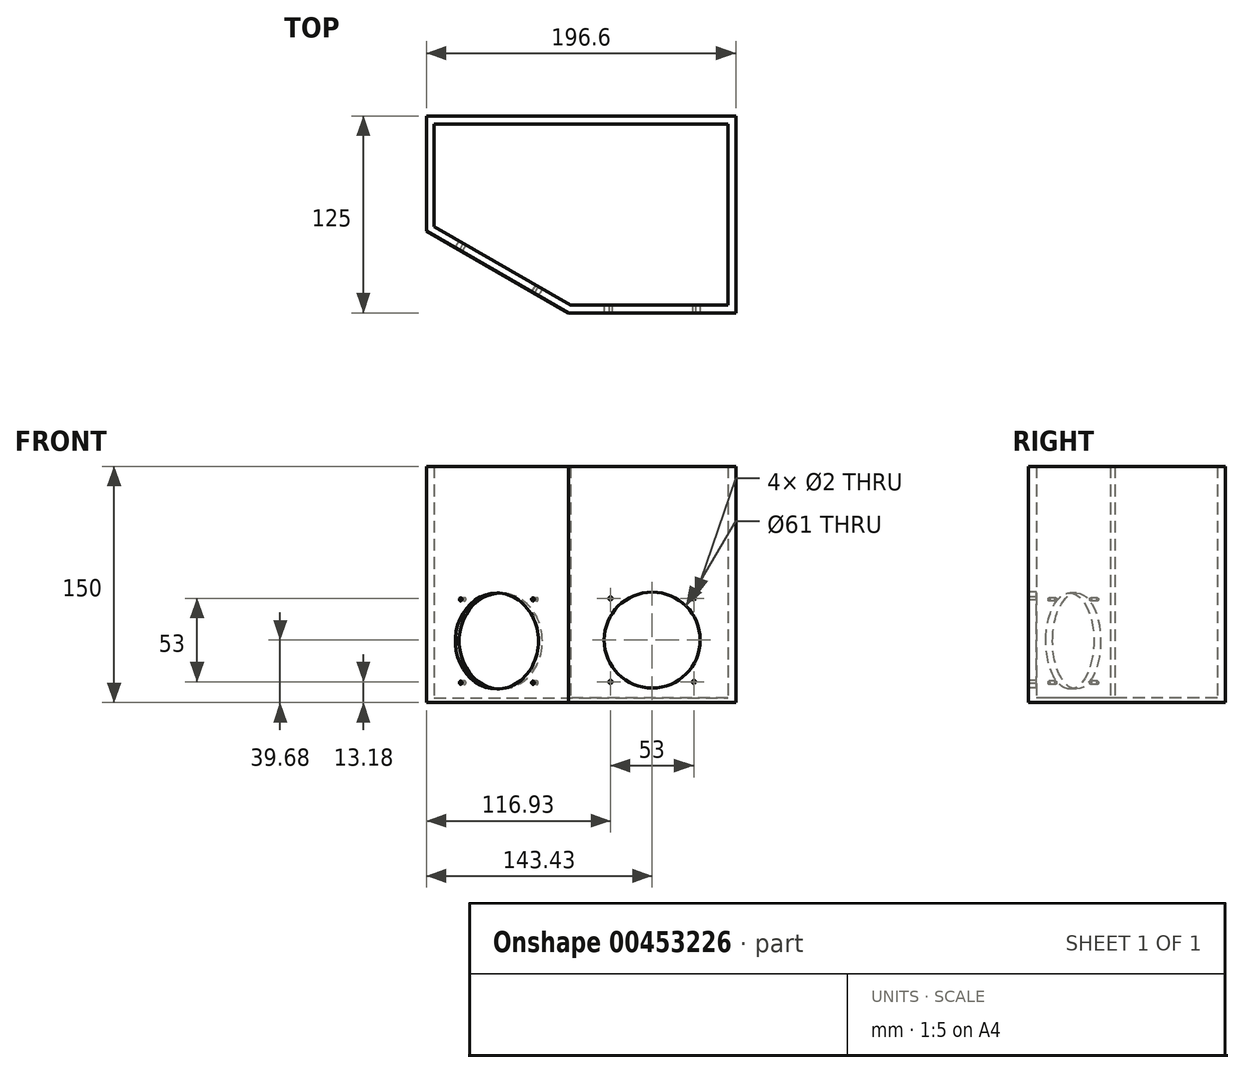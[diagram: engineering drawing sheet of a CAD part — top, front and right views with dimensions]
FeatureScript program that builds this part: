
annotation { "Feature Type Name" : "Feature", "Feature Type Description" : "" }
export const myFeature = defineFeature(function(context is Context, id is Id, definition is map)
    precondition{}
    {
        {
            var Q0;
            Q0=qCreatedBy(makeId("Top.planeOp"),FACE);
            var sketch = newSketch(context, id + "F0", { "sketchPlane" : qUnion([Q0])});
            skLineSegment(sketch, "E0", {"start": v(0, -81.78) * mm, "end": v(100, -81.78) * mm});
            skLineSegment(sketch, "E1", {"start": v(0, -81.78) * mm, "end": v(-86.6, -31.78) * mm});
            skLineSegment(sketch, "E2", {"start": v(100, -81.78) * mm, "end": v(100, 33.22) * mm});
            skLineSegment(sketch, "E3", {"start": v(100, 33.22) * mm, "end": v(-86.6, 33.22) * mm});
            skLineSegment(sketch, "E4", {"start": v(-86.6, -31.78) * mm, "end": v(-86.6, 33.22) * mm});
            skLineSegment(sketch, "E5.0", {"start": v(-91.6, -34.66) * mm, "end": v(-91.6, 38.22) * mm});
            skLineSegment(sketch, "E5.1", {"start": v(105, 38.22) * mm, "end": v(-91.6, 38.22) * mm});
            skLineSegment(sketch, "E5.2", {"start": v(-1.34, -86.78) * mm, "end": v(-91.6, -34.66) * mm});
            skLineSegment(sketch, "E5.3", {"start": v(-1.34, -86.78) * mm, "end": v(105, -86.78) * mm});
            skLineSegment(sketch, "E5.4", {"start": v(105, -86.78) * mm, "end": v(105, 38.22) * mm});
            skSolve(sketch);
        }
        {
            var Q0;
            Q0=makeQuery(id+"F0.imprint","IMPRINT",FACE,{"disambiguationData":[TD([[makeQuery(id+"F0.imprint","IMPRINT",EDGE,{"derivedFrom":sQuery(id+"F0.wireOp",EDGE,"E0")}),1.0]])]});
            var Q1;
            Q1=makeQuery(id+"F0.imprint","IMPRINT",FACE,{"disambiguationData":[TD([[makeQuery(id+"F0.imprint","IMPRINT",EDGE,{"derivedFrom":sQuery(id+"F0.wireOp",EDGE,"E0")}),-1.0]])]});
            extrude(context, id + "F1", {"entities" : qUnion([Q0, Q1]), "depth" : 3 * mm});
        }
        {
            var Q0;
            Q0 = qSketchRegion(id + "F0", true);
            extrude(context, id + "F2", {"entities" : qUnion([Q0]), "operationType" : NewBodyOperationType.ADD, "depth" : 150 * mm});
        }
        {
            var Q0;
            {var subQ0=sQuery(id+"F0.wireOp",EDGE,"E5.3");Q0=makeQuery(id+"F2.boolean.opBoolean","MERGE",FACE,{"derivedFrom":[makeQuery(id+"F1.opExtrude","SWEPT_FACE",FACE,{"disambiguationData":[OSD([subQ0])]}),makeQuery(id+"F2.opExtrude","SWEPT_FACE",FACE,{"disambiguationData":[OSD([subQ0])]})]});}
            var sketch = newSketch(context, id + "F3", { "sketchPlane" : qUnion([Q0])});
            skLineSegment(sketch, "E6", {"start": v(51.83, 0) * mm, "end": v(51.83, 150) * mm, "construction": true});
            skPoint(sketch, "E7", {"position": v(51.83, 39.68) * mm});
            skLineSegment(sketch, "E8.bottom", {"start": v(78.33, 66.18) * mm, "end": v(25.33, 66.18) * mm, "construction": true});
            skLineSegment(sketch, "E8.top", {"start": v(78.33, 13.18) * mm, "end": v(25.33, 13.18) * mm, "construction": true});
            skLineSegment(sketch, "E8.left", {"start": v(78.33, 66.18) * mm, "end": v(78.33, 13.18) * mm, "construction": true});
            skLineSegment(sketch, "E8.right", {"start": v(25.33, 66.18) * mm, "end": v(25.33, 13.18) * mm, "construction": true});
            skCircle(sketch, "E9", {"center": v(78.33, 66.18) * mm, "radius": 1 * mm});
            skCircle(sketch, "E10", {"center": v(78.33, 13.18) * mm, "radius": 1 * mm});
            skCircle(sketch, "E11", {"center": v(25.33, 13.18) * mm, "radius": 1 * mm});
            skCircle(sketch, "E12", {"center": v(25.33, 66.18) * mm, "radius": 1 * mm});
            skCircle(sketch, "E13", {"center": v(51.83, 39.68) * mm, "radius": 30.5 * mm});
            skLineSegment(sketch, "E14", {"start": v(51.83, 39.68) * mm, "end": v(-1.34, 39.68) * mm, "construction": true});
            skLineSegment(sketch, "E15.MirrorCS", {"start": v(51.83, 39.68) * mm, "end": v(105, 39.68) * mm, "construction": true});
            skSolve(sketch);
        }
        {
            var Q0;
            Q0=makeQuery(id+"F3.imprint","IMPRINT",FACE,{"disambiguationData":[TD([[makeQuery(id+"F3.imprint","IMPRINT",EDGE,{"derivedFrom":sQuery(id+"F3.wireOp",EDGE,"E13")}),1.0]])]});
            var Q1;
            Q1=makeQuery(id+"F3.imprint","IMPRINT",FACE,{"disambiguationData":[TD([[makeQuery(id+"F3.imprint","IMPRINT",EDGE,{"derivedFrom":sQuery(id+"F3.wireOp",EDGE,"E11")}),1.0]])]});
            var Q2;
            Q2=makeQuery(id+"F3.imprint","IMPRINT",FACE,{"disambiguationData":[TD([[makeQuery(id+"F3.imprint","IMPRINT",EDGE,{"derivedFrom":sQuery(id+"F3.wireOp",EDGE,"E10")}),1.0]])]});
            var Q3;
            Q3=makeQuery(id+"F3.imprint","IMPRINT",FACE,{"disambiguationData":[TD([[makeQuery(id+"F3.imprint","IMPRINT",EDGE,{"derivedFrom":sQuery(id+"F3.wireOp",EDGE,"E9")}),1.0]])]});
            var Q4;
            Q4=makeQuery(id+"F3.imprint","IMPRINT",FACE,{"disambiguationData":[TD([[makeQuery(id+"F3.imprint","IMPRINT",EDGE,{"derivedFrom":sQuery(id+"F3.wireOp",EDGE,"E12")}),1.0]])]});
            extrude(context, id + "F4", {"entities" : qUnion([Q0, Q1, Q2, Q3, Q4]), "operationType" : NewBodyOperationType.REMOVE, "oppositeDirection" : true, "depth" : 5 * mm});
        }
        {
            var Q0;
            {var subQ0=sQuery(id+"F0.wireOp",EDGE,"E5.2");Q0=makeQuery(id+"F2.boolean.opBoolean","MERGE",FACE,{"derivedFrom":[makeQuery(id+"F1.opExtrude","SWEPT_FACE",FACE,{"disambiguationData":[OSD([subQ0])]}),makeQuery(id+"F2.opExtrude","SWEPT_FACE",FACE,{"disambiguationData":[OSD([subQ0])]})]});}
            var sketch = newSketch(context, id + "F5", { "sketchPlane" : qUnion([Q0])});
            skLineSegment(sketch, "E16", {"start": v(-9.88, 150) * mm, "end": v(-9.88, 0) * mm, "construction": true});
            skLineSegment(sketch, "E17", {"start": v(42.23, 39.1) * mm, "end": v(-62, 39.1) * mm, "construction": true});
            skLineSegment(sketch, "E18", {"start": v(-10.33, -0.57) * mm, "end": v(-10.33, 149.43) * mm, "construction": true});
            skPoint(sketch, "E19", {"position": v(-10.33, 39.1) * mm});
            skLineSegment(sketch, "E20.bottom", {"start": v(16.17, 65.6) * mm, "end": v(-36.83, 65.6) * mm, "construction": true});
            skLineSegment(sketch, "E20.top", {"start": v(16.17, 12.6) * mm, "end": v(-36.83, 12.6) * mm, "construction": true});
            skLineSegment(sketch, "E20.left", {"start": v(16.17, 65.6) * mm, "end": v(16.17, 12.6) * mm, "construction": true});
            skLineSegment(sketch, "E20.right", {"start": v(-36.83, 65.6) * mm, "end": v(-36.83, 12.6) * mm, "construction": true});
            skCircle(sketch, "E21", {"center": v(16.17, 65.6) * mm, "radius": 1 * mm});
            skCircle(sketch, "E22", {"center": v(16.17, 12.6) * mm, "radius": 1 * mm});
            skCircle(sketch, "E23", {"center": v(-36.83, 12.6) * mm, "radius": 1 * mm});
            skCircle(sketch, "E24", {"center": v(-36.83, 65.6) * mm, "radius": 1 * mm});
            skCircle(sketch, "E25", {"center": v(-10.33, 39.1) * mm, "radius": 30.5 * mm});
            skLineSegment(sketch, "E26", {"start": v(-10.33, 39.1) * mm, "end": v(-63.86, 39.1) * mm, "construction": true});
            skLineSegment(sketch, "E27.MirrorCS", {"start": v(-10.33, 39.1) * mm, "end": v(43.2, 39.1) * mm, "construction": true});
            skSolve(sketch);
        }
        {
            var Q0;
            Q0=makeQuery(id+"F5.imprint","IMPRINT",FACE,{"disambiguationData":[TD([[makeQuery(id+"F5.imprint","IMPRINT",EDGE,{"derivedFrom":sQuery(id+"F5.wireOp",EDGE,"E25")}),1.0]])]});
            var Q1;
            Q1=makeQuery(id+"F5.imprint","IMPRINT",FACE,{"disambiguationData":[TD([[makeQuery(id+"F5.imprint","IMPRINT",EDGE,{"derivedFrom":sQuery(id+"F5.wireOp",EDGE,"E21")}),1.0]])]});
            var Q2;
            Q2=makeQuery(id+"F5.imprint","IMPRINT",FACE,{"disambiguationData":[TD([[makeQuery(id+"F5.imprint","IMPRINT",EDGE,{"derivedFrom":sQuery(id+"F5.wireOp",EDGE,"E22")}),1.0]])]});
            var Q3;
            Q3=makeQuery(id+"F5.imprint","IMPRINT",FACE,{"disambiguationData":[TD([[makeQuery(id+"F5.imprint","IMPRINT",EDGE,{"derivedFrom":sQuery(id+"F5.wireOp",EDGE,"E24")}),1.0]])]});
            var Q4;
            Q4=makeQuery(id+"F5.imprint","IMPRINT",FACE,{"disambiguationData":[TD([[makeQuery(id+"F5.imprint","IMPRINT",EDGE,{"derivedFrom":sQuery(id+"F5.wireOp",EDGE,"E23")}),1.0]])]});
            extrude(context, id + "F6", {"entities" : qUnion([Q0, Q1, Q2, Q3, Q4]), "operationType" : NewBodyOperationType.REMOVE, "oppositeDirection" : true, "depth" : 5 * mm});
        }
    });
